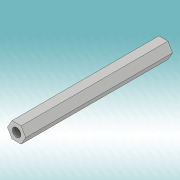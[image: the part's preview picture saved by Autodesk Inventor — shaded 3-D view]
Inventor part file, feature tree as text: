
AUTODESK INVENTOR PART (.ipt)
format: ipt  version: 2019 (Build 230136000, 136)  size: 103,424 bytes
history: native  units: mm
features: extrude x1, thread x1, sketch x1
ambient origin geometry x8: Origin, YZ Plane, XZ Plane, XY Plane, X Axis, Y Axis, Z Axis, Center Point
bodies: Solid1 (feature_tree)
feature tree (3):
  extrude  "Extrusion1"  Depth=10.0mm
  thread  "Thread3"  [1 undecoded]
  sketch  "Sketch1"  dims[d1=5.5mm d2=1.0mm d3=1.0mm d4=51.0mm d5=0.0mm d7=3.0mm d12=10.0mm d13=0.0mm]
note: 1 required parameter value undecoded (feature->parameter linkage not recoverable at this tier; creation-order binding heuristic only, values carry confidence <= 0.55)
